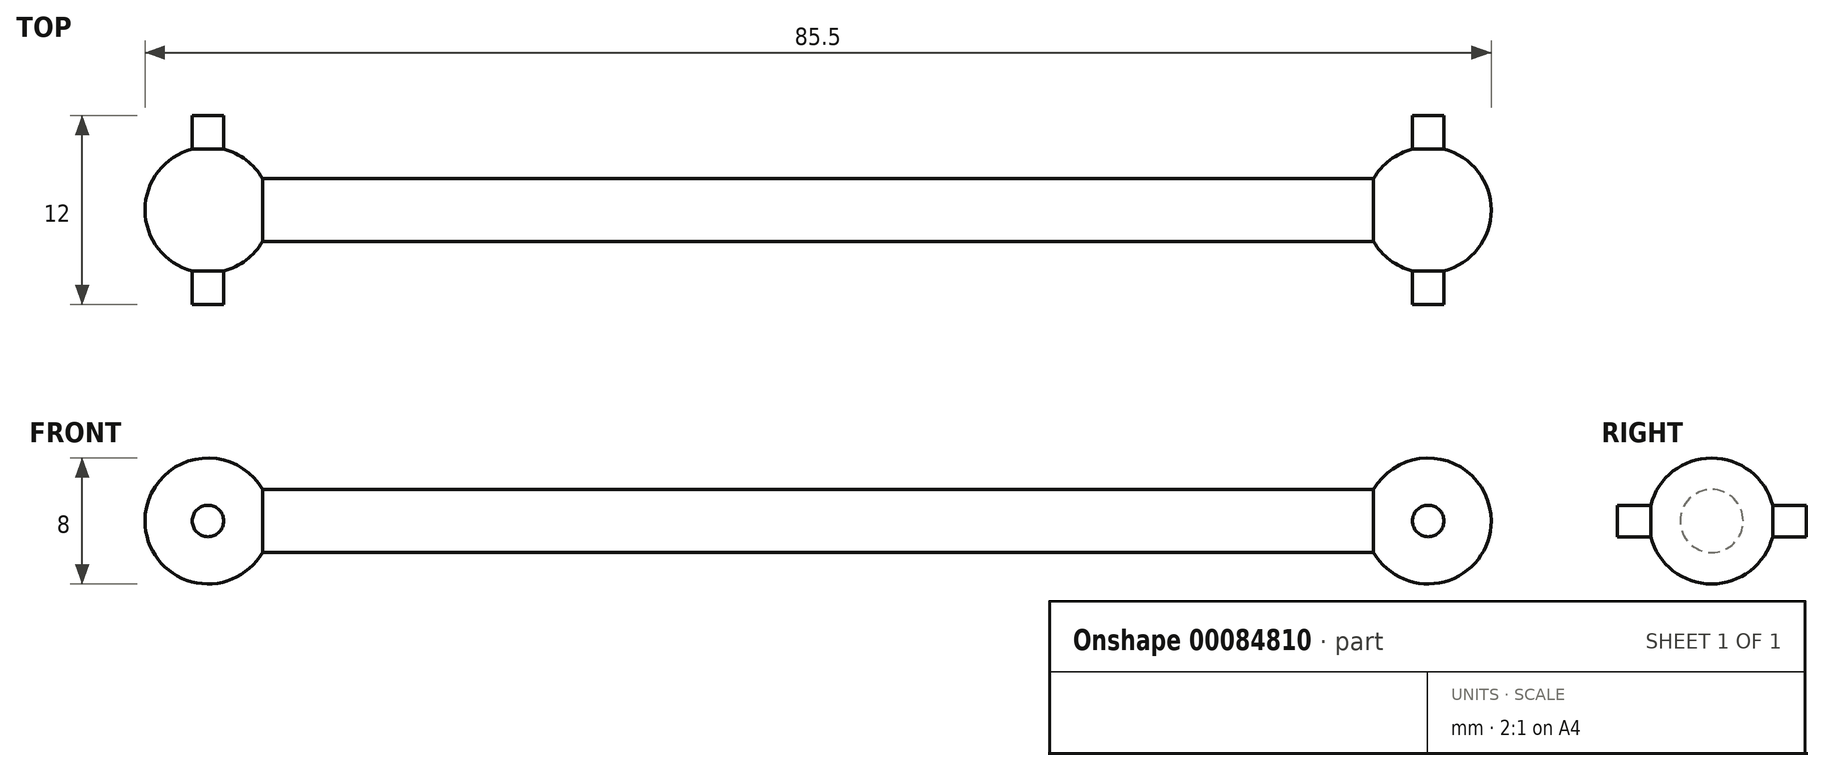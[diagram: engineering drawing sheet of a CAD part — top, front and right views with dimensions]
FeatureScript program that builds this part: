
annotation { "Feature Type Name" : "Feature", "Feature Type Description" : "" }
export const myFeature = defineFeature(function(context is Context, id is Id, definition is map)
    precondition{}
    {
        {
            var Q0;
            Q0=qCreatedBy(makeId("Front.planeOp"),FACE);
            var sketch = newSketch(context, id + "F0", { "sketchPlane" : qUnion([Q0])});
            skLineSegment(sketch, "E0", {"start": v(-45.32, 0) * mm, "end": v(40.18, 0) * mm, "construction": true});
            skArc(sketch, "E1", {"start": v(-37.86, 2) * mm, "mid": v(-42.36, 3.86) * mm, "end": v(-45.32, 0) * mm});
            skArc(sketch, "E2", {"start": v(40.18, 0) * mm, "mid": v(37.21, 3.86) * mm, "end": v(32.71, 2) * mm});
            skLineSegment(sketch, "E3", {"start": v(-37.86, 2) * mm, "end": v(32.71, 2) * mm});
            skLineSegment(sketch, "E4", {"start": v(-41.32, 2) * mm, "end": v(-41.32, 0) * mm, "construction": true});
            skLineSegment(sketch, "E5", {"start": v(36.18, 2) * mm, "end": v(36.18, 0) * mm, "construction": true});
            skLineSegment(sketch, "E6", {"start": v(-45.32, 0) * mm, "end": v(40.18, 0) * mm});
            skSolve(sketch);
        }
        {
            var Q0;
            {var subQ0=sQuery(id+"F0.wireOp",EDGE,"E6");var subQ1=sQuery(id+"F0.wireOp",EDGE,"E1");var subQ2=makeQuery(id+"F0.imprint","INTERSECT",VERTEX,{"disambiguationData":[OD(0.0)],"derivedFrom":[subQ1,subQ0]});Q0=makeQuery(id+"F0.imprint","IMPRINT",FACE,{"disambiguationData":[TD([[makeQuery(id+"F0.imprint","IMPRINT",EDGE,{"disambiguationData":[TD([[subQ2,-1.0]])],"derivedFrom":subQ1}),1.0]])]});}
            var Q1;
            {var subQ0=sQuery(id+"F0.wireOp",EDGE,"E6");var subQ1=sQuery(id+"F0.wireOp",EDGE,"E2");var subQ2=makeQuery(id+"F0.imprint","INTERSECT",VERTEX,{"disambiguationData":[OD(0.0)],"derivedFrom":[subQ1,subQ0]});Q1=makeQuery(id+"F0.imprint","IMPRINT",FACE,{"disambiguationData":[TD([[makeQuery(id+"F0.imprint","IMPRINT",EDGE,{"disambiguationData":[TD([[subQ2,-1.0]])],"derivedFrom":subQ1}),1.0]])]});}
            var Q2;
            Q2=sQuery(id+"F0.wireOp",EDGE,"E6");
            revolve(context, id + "F1", {"entities" : qUnion([Q0, Q1]), "axis" : qUnion([Q2]), "revolveType" : RevolveType.FULL});
        }
        {
            var Q0;
            Q0=qCreatedBy(makeId("Front.planeOp"),FACE);
            var sketch = newSketch(context, id + "F2", { "sketchPlane" : qUnion([Q0])});
            skCircle(sketch, "E7", {"center": v(-41.32, 0) * mm, "radius": 1 * mm});
            skCircle(sketch, "E8", {"center": v(36.18, 0) * mm, "radius": 1 * mm});
            skLineSegment(sketch, "E9", {"start": v(-41.32, 0) * mm, "end": v(36.18, 0) * mm, "construction": true});
            skSolve(sketch);
        }
        {
            var Q0;
            Q0 = qSketchRegion(id + "F2", true);
            extrude(context, id + "F3", {"entities" : qUnion([Q0]), "operationType" : NewBodyOperationType.ADD, "endBound" : BoundingType.SYMMETRIC, "depth" : 12 * mm});
        }
    });
